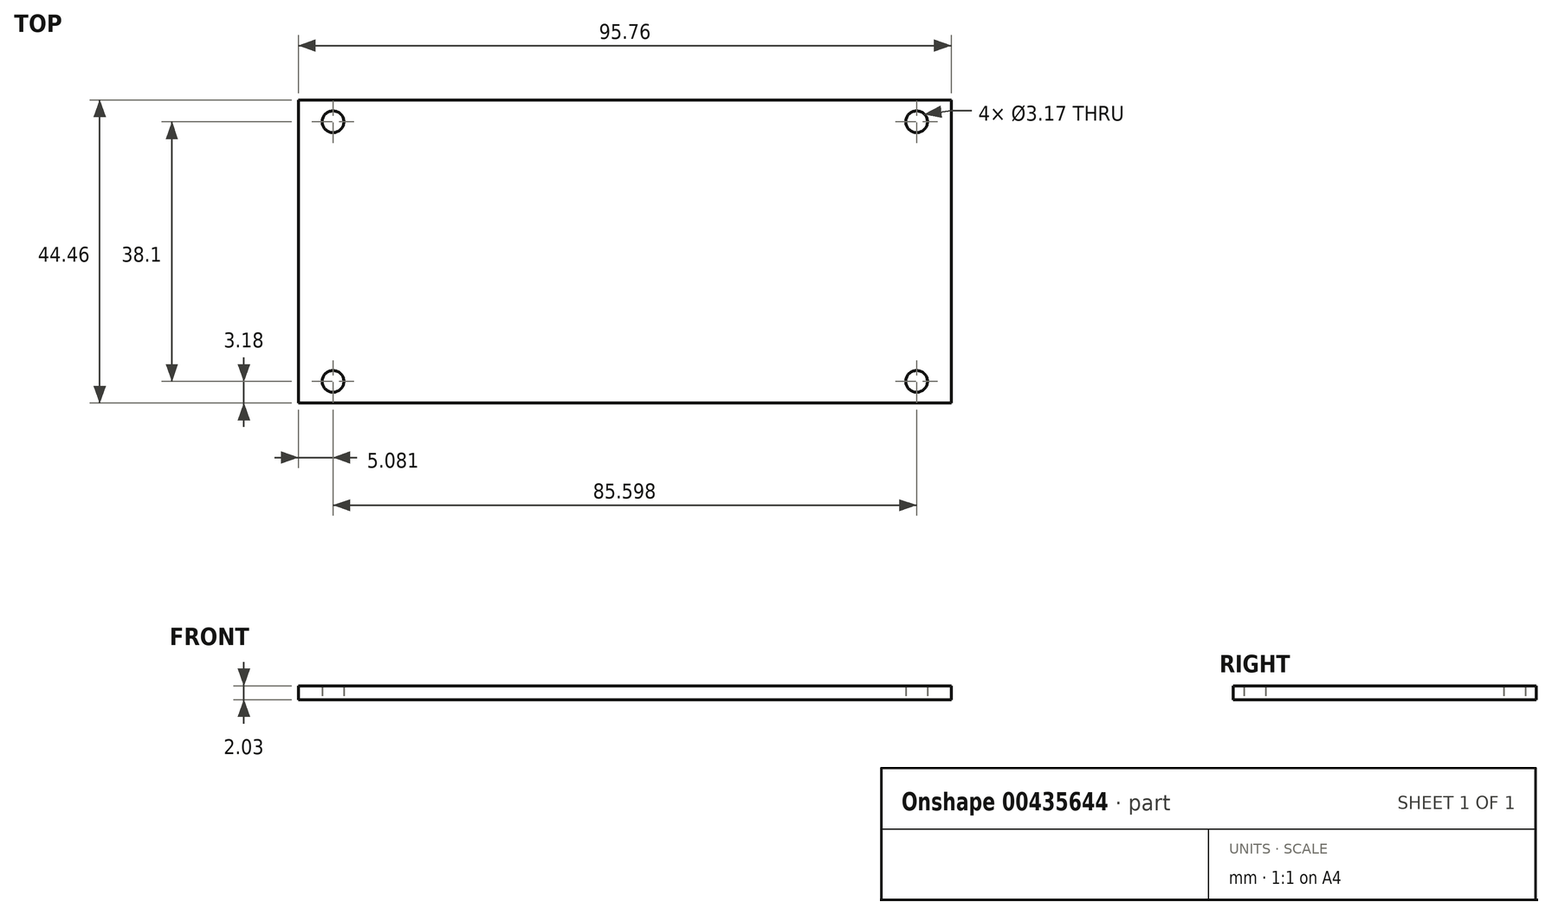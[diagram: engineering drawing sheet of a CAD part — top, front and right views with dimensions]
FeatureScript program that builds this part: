
annotation { "Feature Type Name" : "Feature", "Feature Type Description" : "" }
export const myFeature = defineFeature(function(context is Context, id is Id, definition is map)
    precondition{}
    {
        {
            var Q0;
            Q0=qCreatedBy(makeId("Top.planeOp"),FACE);
            var sketch = newSketch(context, id + "F0", { "sketchPlane" : qUnion([Q0])});
            skLineSegment(sketch, "E0.bottom", {"start": v(-47.88, 22.22) * mm, "end": v(47.88, 22.22) * mm});
            skLineSegment(sketch, "E0.top", {"start": v(-47.88, -22.22) * mm, "end": v(47.88, -22.22) * mm});
            skLineSegment(sketch, "E0.left", {"start": v(-47.88, 22.22) * mm, "end": v(-47.88, -22.22) * mm});
            skLineSegment(sketch, "E0.right", {"start": v(47.88, 22.22) * mm, "end": v(47.88, -22.22) * mm});
            skLineSegment(sketch, "E1", {"start": v(-47.88, 22.23) * mm, "end": v(47.88, -22.23) * mm, "construction": true});
            skLineSegment(sketch, "E2", {"start": v(47.88, 22.23) * mm, "end": v(-47.88, -22.22) * mm, "construction": true});
            skCircle(sketch, "E3", {"center": v(-42.8, 19.05) * mm, "radius": 1.59 * mm});
            skCircle(sketch, "E4", {"center": v(-42.8, -19.05) * mm, "radius": 1.59 * mm});
            skCircle(sketch, "E5", {"center": v(42.8, -19.05) * mm, "radius": 1.59 * mm});
            skCircle(sketch, "E6", {"center": v(42.8, 19.05) * mm, "radius": 1.59 * mm});
            skSolve(sketch);
        }
        {
            var Q0;
            Q0 = qSketchRegion(id + "F0", true);
            extrude(context, id + "F1", {"entities" : qUnion([Q0]), "depth" : 2.03 * mm});
        }
    });
